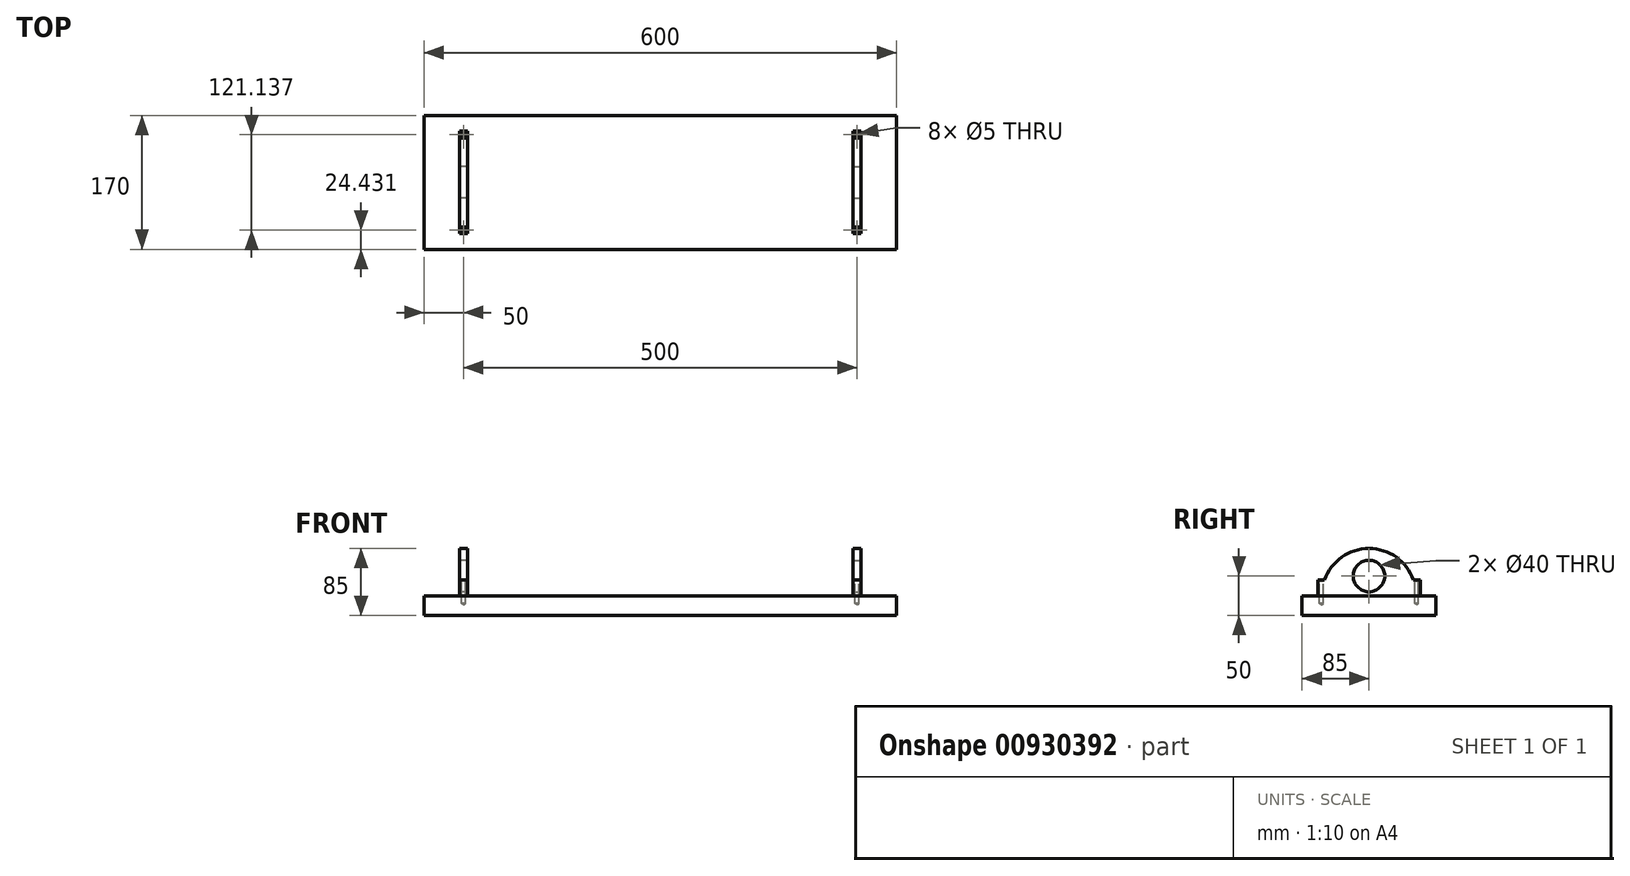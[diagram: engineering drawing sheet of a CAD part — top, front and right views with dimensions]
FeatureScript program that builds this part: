
annotation { "Feature Type Name" : "Feature", "Feature Type Description" : "" }
export const myFeature = defineFeature(function(context is Context, id is Id, definition is map)
    precondition{}
    {
        {
            var Q0;
            Q0=qCreatedBy(makeId("Top.planeOp"),FACE);
            var sketch = newSketch(context, id + "F0", { "sketchPlane" : qUnion([Q0])});
            skLineSegment(sketch, "E0.bottom", {"start": v(300, -85) * mm, "end": v(-300, -85) * mm});
            skLineSegment(sketch, "E0.top", {"start": v(300, 85) * mm, "end": v(-300, 85) * mm});
            skLineSegment(sketch, "E0.left", {"start": v(300, -85) * mm, "end": v(300, 85) * mm});
            skLineSegment(sketch, "E0.right", {"start": v(-300, -85) * mm, "end": v(-300, 85) * mm});
            skPoint(sketch, "E0.middle", {"position": v(0, 0) * mm});
            skSolve(sketch);
        }
        {
            var Q0;
            Q0 = qSketchRegion(id + "F0", true);
            extrude(context, id + "F1", {"entities" : qUnion([Q0]), "depth" : 25 * mm, "offsetDistance" : 25 * mm});
        }
        {
            var Q0;
            Q0=qCreatedBy(makeId("Right.planeOp"),FACE);
            var sketch = newSketch(context, id + "F2", { "sketchPlane" : qUnion([Q0])});
            skLineSegment(sketch, "E1", {"start": v(65, 25) * mm, "end": v(65, 45) * mm});
            skLineSegment(sketch, "E2", {"start": v(65, 45) * mm, "end": v(56.57, 45) * mm});
            skLineSegment(sketch, "E3.MirrorCS", {"start": v(-65, 45) * mm, "end": v(-56.57, 45) * mm});
            skLineSegment(sketch, "E4.MirrorCS", {"start": v(-65, 25) * mm, "end": v(-65, 45) * mm});
            skLineSegment(sketch, "E5", {"start": v(65, 25) * mm, "end": v(-65, 25) * mm});
            skArc(sketch, "E6", {"start": v(56.57, 45) * mm, "mid": v(0, 85) * mm, "end": v(-56.57, 45) * mm});
            skSolve(sketch);
        }
        {
            var Q0;
            Q0 = qSketchRegion(id + "F2", true);
            extrude(context, id + "F3", {"entities" : qUnion([Q0]), "endBound" : BoundingType.SYMMETRIC, "depth" : 10 * mm, "offsetDistance" : 25 * mm});
        }
        {
            var Q0;
            Q0=makeQuery(id+"F3.opExtrude","SWEPT_BODY",BODY,{"disambiguationData":[OSD([sQuery(id+"F2.wireOp",EDGE,"E1"),sQuery(id+"F2.wireOp",EDGE,"E2"),sQuery(id+"F2.wireOp",EDGE,"E3.MirrorCS"),sQuery(id+"F2.wireOp",EDGE,"E4.MirrorCS"),sQuery(id+"F2.wireOp",EDGE,"E5"),sQuery(id+"F2.wireOp",EDGE,"E6")])]});
            transform(context, id + "F4", {"entities" : qUnion([Q0]), "transformType" : TransformType.TRANSLATION_3D, "dx" : -250 * mm, "dy" : 0 * mm, "dz" : 0 * mm, "makeCopy" : true});
        }
        {
            var Q0;
            Q0=makeQuery(id+"F3.opExtrude","SWEPT_BODY",BODY,{"disambiguationData":[OSD([sQuery(id+"F2.wireOp",EDGE,"E1"),sQuery(id+"F2.wireOp",EDGE,"E2"),sQuery(id+"F2.wireOp",EDGE,"E3.MirrorCS"),sQuery(id+"F2.wireOp",EDGE,"E4.MirrorCS"),sQuery(id+"F2.wireOp",EDGE,"E5"),sQuery(id+"F2.wireOp",EDGE,"E6")])]});
            transform(context, id + "F5", {"entities" : qUnion([Q0]), "transformType" : TransformType.TRANSLATION_3D, "dx" : 250 * mm, "dy" : 0 * mm, "dz" : 0 * mm, "makeCopy" : false});
        }
        {
            var Q0;
            Q0=makeQuery(id+"F4.opPattern","COPY",FACE,{"derivedFrom":makeQuery(id+"F3.opExtrude","CAP_FACE",FACE,{"disambiguationData":[OSD([sQuery(id+"F2.wireOp",EDGE,"E1"),sQuery(id+"F2.wireOp",EDGE,"E2"),sQuery(id+"F2.wireOp",EDGE,"E3.MirrorCS"),sQuery(id+"F2.wireOp",EDGE,"E4.MirrorCS"),sQuery(id+"F2.wireOp",EDGE,"E5"),sQuery(id+"F2.wireOp",EDGE,"E6")])],"isStart":true}),"instanceName":"1"});
            var sketch = newSketch(context, id + "F6", { "sketchPlane" : qUnion([Q0])});
            skCircle(sketch, "E7", {"center": v(0, 50) * mm, "radius": 20 * mm});
            skSolve(sketch);
        }
        {
            var Q0;
            Q0 = qSketchRegion(id + "F6", true);
            extrude(context, id + "F7", {"entities" : qUnion([Q0]), "operationType" : NewBodyOperationType.REMOVE, "oppositeDirection" : true, "depth" : 10 * mm, "offsetDistance" : 25 * mm});
        }
        {
            var Q0;
            Q0=makeQuery(id+"F3.opExtrude","CAP_FACE",FACE,{"disambiguationData":[OSD([sQuery(id+"F2.wireOp",EDGE,"E1"),sQuery(id+"F2.wireOp",EDGE,"E2"),sQuery(id+"F2.wireOp",EDGE,"E3.MirrorCS"),sQuery(id+"F2.wireOp",EDGE,"E4.MirrorCS"),sQuery(id+"F2.wireOp",EDGE,"E5"),sQuery(id+"F2.wireOp",EDGE,"E6")])],"isStart":false});
            var sketch = newSketch(context, id + "F8", { "sketchPlane" : qUnion([Q0])});
            skCircle(sketch, "E8", {"center": v(0, 50) * mm, "radius": 20 * mm});
            skSolve(sketch);
        }
        {
            var Q0;
            Q0 = qSketchRegion(id + "F8", true);
            extrude(context, id + "F9", {"entities" : qUnion([Q0]), "operationType" : NewBodyOperationType.REMOVE, "oppositeDirection" : true, "depth" : 10 * mm, "offsetDistance" : 25 * mm});
        }
        {
            var Q0;
            Q0=makeQuery(id+"F4.opPattern","COPY",FACE,{"derivedFrom":makeQuery(id+"F3.opExtrude","SWEPT_FACE",FACE,{"disambiguationData":[OSD([sQuery(id+"F2.wireOp",EDGE,"E2")])]}),"instanceName":"1"});
            var sketch = newSketch(context, id + "F10", { "sketchPlane" : qUnion([Q0])});
            skPoint(sketch, "E9", {"position": v(-250, 60.57) * mm});
            skPoint(sketch, "E10.MirrorP", {"position": v(250, 60.57) * mm});
            skPoint(sketch, "E11.MirrorP", {"position": v(-250, -60.57) * mm});
            skPoint(sketch, "E12.MirrorP", {"position": v(250, -60.57) * mm});
            skCircle(sketch, "E13", {"center": v(-250, 60.57) * mm, "radius": 2.5 * mm});
            skCircle(sketch, "E14.MirrorC", {"center": v(-250, -60.57) * mm, "radius": 2.5 * mm});
            skCircle(sketch, "E15.MirrorC", {"center": v(250, 60.57) * mm, "radius": 2.5 * mm});
            skCircle(sketch, "E16.MirrorC", {"center": v(250, -60.57) * mm, "radius": 2.5 * mm});
            skSolve(sketch);
        }
        {
            var Q0;
            Q0=sQuery(id+"F10.wireOp",VERTEX,"E9");
            var Q1;
            Q1=sQuery(id+"F10.wireOp",VERTEX,"E11.MirrorP");
            var Q2;
            Q2=makeQuery(id+"F4.opPattern","COPY",BODY,{"derivedFrom":makeQuery(id+"F3.opExtrude","SWEPT_BODY",BODY,{"disambiguationData":[OSD([sQuery(id+"F2.wireOp",EDGE,"E1"),sQuery(id+"F2.wireOp",EDGE,"E2"),sQuery(id+"F2.wireOp",EDGE,"E3.MirrorCS"),sQuery(id+"F2.wireOp",EDGE,"E4.MirrorCS"),sQuery(id+"F2.wireOp",EDGE,"E5"),sQuery(id+"F2.wireOp",EDGE,"E6")])]}),"instanceName":"1"});
            var Q3;
            Q3=makeQuery(id+"F1.opExtrude","SWEPT_BODY",BODY,{"disambiguationData":[OSD([sQuery(id+"F0.wireOp",EDGE,"E0.bottom"),sQuery(id+"F0.wireOp",EDGE,"E0.top"),sQuery(id+"F0.wireOp",EDGE,"E0.left"),sQuery(id+"F0.wireOp",EDGE,"E0.right")])]});
            hole(context, id + "F11", {"style" : HoleStyle.C_SINK, "endStyle" : HoleEndStyle.BLIND, "holeDiameter" : 5 * mm, "cSinkDiameter" : 7 * mm, "cSinkAngle" : 90 * degree, "majorDiameter" : 5 * mm, "holeDepth" : 30 * mm, "isTappedThrough" : true, "tappedDepth" : 12 * mm, "tapClearance" : 3, "startFromSketch" : true, "locations" : qUnion([Q0, Q1]), "scope" : qUnion([Q2, Q3])});
        }
        {
            var Q0;
            Q0=makeQuery(id+"F4.opPattern","COPY",FACE,{"derivedFrom":makeQuery(id+"F3.opExtrude","SWEPT_FACE",FACE,{"disambiguationData":[OSD([sQuery(id+"F2.wireOp",EDGE,"E2")])]}),"instanceName":"1"});
            var sketch = newSketch(context, id + "F12", { "sketchPlane" : qUnion([Q0])});
            skCircle(sketch, "E17.0", {"center": v(-250, 60.57) * mm, "radius": 3.5 * mm});
            skSolve(sketch);
        }
        {
            var Q0;
            Q0 = qSketchRegion(id + "F12", true);
            var Q1;
            Q1=makeQuery(id+"F1.opExtrude","CAP_FACE",FACE,{"disambiguationData":[OSD([sQuery(id+"F0.wireOp",EDGE,"E0.bottom"),sQuery(id+"F0.wireOp",EDGE,"E0.top"),sQuery(id+"F0.wireOp",EDGE,"E0.left"),sQuery(id+"F0.wireOp",EDGE,"E0.right")])],"isStart":true});
            extrude(context, id + "F13", {"entities" : qUnion([Q0]), "endBound" : BoundingType.UP_TO_SURFACE, "oppositeDirection" : true, "depth" : 25 * mm, "endBoundEntityFace" : qUnion([Q1]), "offsetDistance" : 25 * mm});
        }
        {
            var Q0;
            Q0=makeQuery(id+"F1.opExtrude","SWEPT_BODY",BODY,{"disambiguationData":[OSD([sQuery(id+"F0.wireOp",EDGE,"E0.bottom"),sQuery(id+"F0.wireOp",EDGE,"E0.top"),sQuery(id+"F0.wireOp",EDGE,"E0.left"),sQuery(id+"F0.wireOp",EDGE,"E0.right")])]});
            var Q1;
            Q1=makeQuery(id+"F4.opPattern","COPY",BODY,{"derivedFrom":makeQuery(id+"F3.opExtrude","SWEPT_BODY",BODY,{"disambiguationData":[OSD([sQuery(id+"F2.wireOp",EDGE,"E1"),sQuery(id+"F2.wireOp",EDGE,"E2"),sQuery(id+"F2.wireOp",EDGE,"E3.MirrorCS"),sQuery(id+"F2.wireOp",EDGE,"E4.MirrorCS"),sQuery(id+"F2.wireOp",EDGE,"E5"),sQuery(id+"F2.wireOp",EDGE,"E6")])]}),"instanceName":"1"});
            var Q2;
            Q2=makeQuery(id+"F13.opExtrude","SWEPT_BODY",BODY,{"disambiguationData":[OSD([sQuery(id+"F12.wireOp",EDGE,"E17.0")])]});
            booleanBodies(context, id + "F14", {"operationType" : BooleanOperationType.SUBTRACTION, "tools" : qUnion([Q0, Q1]), "targets" : qUnion([Q2]), "keepTools" : true});
        }
        {
            var Q0;
            Q0=makeQuery(id+"F3.opExtrude","SWEPT_FACE",FACE,{"disambiguationData":[OSD([sQuery(id+"F2.wireOp",EDGE,"E2")])]});
            var sketch = newSketch(context, id + "F15", { "sketchPlane" : qUnion([Q0])});
            skPoint(sketch, "E18", {"position": v(250, 60.57) * mm});
            skCircle(sketch, "E19", {"center": v(250, 60.57) * mm, "radius": 2.5 * mm});
            skCircle(sketch, "E20.MirrorC", {"center": v(250, -60.57) * mm, "radius": 2.5 * mm});
            skSolve(sketch);
        }
        {
            var Q0;
            Q0=sQuery(id+"F15.wireOp",VERTEX,"E18");
            var Q1;
            Q1=sQuery(id+"F15.wireOp",VERTEX,"E20.MirrorC.center");
            var Q2;
            Q2=makeQuery(id+"F3.opExtrude","SWEPT_BODY",BODY,{"disambiguationData":[OSD([sQuery(id+"F2.wireOp",EDGE,"E1"),sQuery(id+"F2.wireOp",EDGE,"E2"),sQuery(id+"F2.wireOp",EDGE,"E3.MirrorCS"),sQuery(id+"F2.wireOp",EDGE,"E4.MirrorCS"),sQuery(id+"F2.wireOp",EDGE,"E5"),sQuery(id+"F2.wireOp",EDGE,"E6")])]});
            var Q3;
            Q3=makeQuery(id+"F1.opExtrude","SWEPT_BODY",BODY,{"disambiguationData":[OSD([sQuery(id+"F0.wireOp",EDGE,"E0.bottom"),sQuery(id+"F0.wireOp",EDGE,"E0.top"),sQuery(id+"F0.wireOp",EDGE,"E0.left"),sQuery(id+"F0.wireOp",EDGE,"E0.right")])]});
            hole(context, id + "F16", {"style" : HoleStyle.C_SINK, "endStyle" : HoleEndStyle.BLIND, "holeDiameter" : 5 * mm, "cSinkDiameter" : 7 * mm, "cSinkAngle" : 90 * degree, "majorDiameter" : 5 * mm, "holeDepth" : 30 * mm, "isTappedThrough" : true, "tappedDepth" : 12 * mm, "tapClearance" : 3, "startFromSketch" : true, "locations" : qUnion([Q0, Q1]), "scope" : qUnion([Q2, Q3])});
        }
    });
